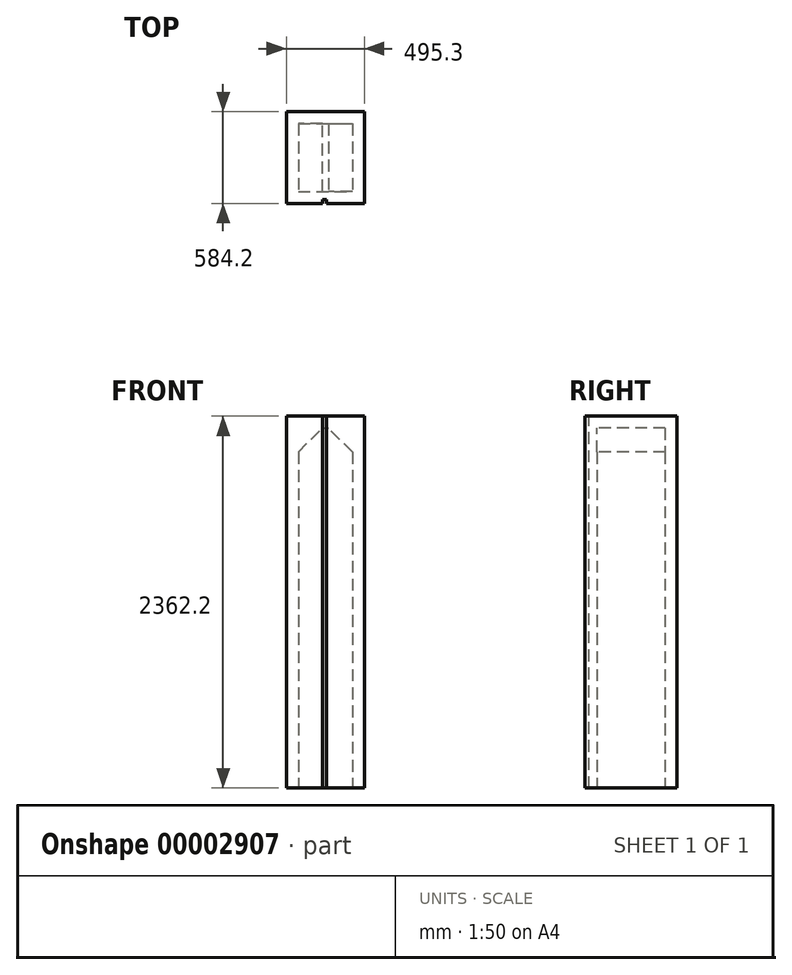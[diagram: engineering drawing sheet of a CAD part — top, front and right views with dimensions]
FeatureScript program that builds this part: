
annotation { "Feature Type Name" : "Feature", "Feature Type Description" : "" }
export const myFeature = defineFeature(function(context is Context, id is Id, definition is map)
    precondition{}
    {
        {
            var Q0;
            Q0=qCreatedBy(makeId("Top.planeOp"),FACE);
            var sketch = newSketch(context, id + "F0", { "sketchPlane" : qUnion([Q0])});
            skLineSegment(sketch, "E0.bottom", {"start": v(-242.5, 368.13) * mm, "end": v(252.8, 368.13) * mm});
            skLineSegment(sketch, "E0.top", {"start": v(-242.5, -216.07) * mm, "end": v(252.8, -216.07) * mm});
            skLineSegment(sketch, "E0.left", {"start": v(-242.5, 368.13) * mm, "end": v(-242.5, -216.07) * mm});
            skLineSegment(sketch, "E0.right", {"start": v(252.8, 368.13) * mm, "end": v(252.8, -216.07) * mm});
            skSolve(sketch);
        }
        {
            var Q0;
            Q0 = qSketchRegion(id + "F0", true);
            extrude(context, id + "F1", {"entities" : qUnion([Q0]), "depth" : 2362.2 * mm});
        }
        {
            var Q0;
            Q0=makeQuery(id+"F1.opExtrude","SWEPT_FACE",FACE,{"disambiguationData":[OSD([sQuery(id+"F0.wireOp",EDGE,"E0.top")])]});
            var sketch = newSketch(context, id + "F2", { "sketchPlane" : qUnion([Q0])});
            skLineSegment(sketch, "E1.bottom", {"start": v(-12.7, 0) * mm, "end": v(12.7, 0) * mm});
            skLineSegment(sketch, "E1.top", {"start": v(-12.7, 2362.2) * mm, "end": v(12.7, 2362.2) * mm});
            skLineSegment(sketch, "E1.left", {"start": v(-12.7, 0) * mm, "end": v(-12.7, 2362.2) * mm});
            skLineSegment(sketch, "E1.right", {"start": v(12.7, 0) * mm, "end": v(12.7, 2362.2) * mm});
            skSolve(sketch);
        }
        {
            var Q0;
            Q0 = qSketchRegion(id + "F2", true);
            extrude(context, id + "F3", {"entities" : qUnion([Q0]), "operationType" : NewBodyOperationType.REMOVE, "oppositeDirection" : true, "depth" : 25.4 * mm});
        }
        {
            var Q0;
            Q0=makeQuery(id+"F1.opExtrude","CAP_FACE",FACE,{"disambiguationData":[OSD([sQuery(id+"F0.wireOp",EDGE,"E0.bottom"),sQuery(id+"F0.wireOp",EDGE,"E0.top"),sQuery(id+"F0.wireOp",EDGE,"E0.left"),sQuery(id+"F0.wireOp",EDGE,"E0.right")])],"isStart":true});
            shell(context, id + "F4", {"entities" : qUnion([Q0]), "thickness" : 76.2 * mm});
        }
        {
            var Q0;
            Q0=makeQuery(id+"F1.opExtrude","CAP_FACE",FACE,{"disambiguationData":[OSD([sQuery(id+"F0.wireOp",EDGE,"E0.bottom"),sQuery(id+"F0.wireOp",EDGE,"E0.top"),sQuery(id+"F0.wireOp",EDGE,"E0.left"),sQuery(id+"F0.wireOp",EDGE,"E0.right")])],"isStart":true});
            var sketch = newSketch(context, id + "F5", { "sketchPlane" : qUnion([Q0])});
            skLineSegment(sketch, "E2.bottom", {"start": v(-88.9, 114.47) * mm, "end": v(88.9, 114.47) * mm});
            skLineSegment(sketch, "E2.top", {"start": v(-88.9, 139.87) * mm, "end": v(88.9, 139.87) * mm});
            skLineSegment(sketch, "E2.left", {"start": v(-88.9, 114.47) * mm, "end": v(-88.9, 139.87) * mm});
            skLineSegment(sketch, "E2.right", {"start": v(88.9, 114.47) * mm, "end": v(88.9, 139.87) * mm});
            skSolve(sketch);
        }
        {
            var Q0;
            Q0 = qSketchRegion(id + "F5", true);
            var Q1;
            Q1=makeQuery(id+"F4.opShell","OFFSET_FACE",FACE,{"disambiguationData":[OSD([sQuery(id+"F0.wireOp",EDGE,"E0.bottom"),sQuery(id+"F0.wireOp",EDGE,"E0.top"),sQuery(id+"F0.wireOp",EDGE,"E0.left"),sQuery(id+"F0.wireOp",EDGE,"E0.right")])]});
            extrude(context, id + "F6", {"entities" : qUnion([Q0]), "operationType" : NewBodyOperationType.REMOVE, "endBound" : BoundingType.UP_TO_SURFACE, "oppositeDirection" : true, "endBoundEntityFace" : qUnion([Q1]), "depth" : 25.4 * mm});
        }
        {
            var Q0;
            {var subQ0=sQuery(id+"F0.wireOp",EDGE,"E0.left");Q0=makeQuery(id+"F4.opShell","OFFSET_EDGE",EDGE,{"disambiguationData":[OSD([subQ0]),TDD([makeQuery(id+"F1.opExtrude","CAP_EDGE",EDGE,{"disambiguationData":[OSD([subQ0])],"isStart":false})])]});}
            var Q1;
            {var subQ0=sQuery(id+"F0.wireOp",EDGE,"E0.right");Q1=makeQuery(id+"F4.opShell","OFFSET_EDGE",EDGE,{"disambiguationData":[OSD([subQ0]),TDD([makeQuery(id+"F1.opExtrude","CAP_EDGE",EDGE,{"disambiguationData":[OSD([subQ0])],"isStart":false})])]});}
            chamfer(context, id + "F7", {"entities" : qUnion([Q0, Q1]), "width" : 152.4 * mm, "tangentPropagation" : true});
        }
    });
